# Revit family: 08101000
name_source: partatom
category: Specialty Equipment
units: mm (PartAtom-declared; Revit-internal decimal feet)

## family parameters
Always vertical = Yes
Cut with Voids When Loaded = No
Enable Cutting in Views = Yes
Maintain Annotation Orientation = No
OmniClass Number = 23.40.40.00
OmniClass Title = Food Service Equipment and Furnishings
Part Type = Normal
Room Calculation Point = No
Round Connector Dimension = Use Diameter
Shared = No
Work Plane-Based = No

## types (1)
- Standard
    Connector_1_Diameter = 24 mm  [stored 0.0787402 ft]
    Default Elevation = 0 mm  [stored 0 ft]
    Description = Kjølt brønn KBK-160-1GN
    Height = 537 mm
    Length = 427 mm
    Manufacturer = Rustfriebergh AS
    Mass = 47,00 kg
    Model = 08101000
    URL = https://www.rustfriebergh.no
    Width = 630 mm

note: [stored X ft] marks values corroborated as IEEE doubles in the binary element streams (Revit-internal decimal feet)

## geometry (parser evidence)
native form markers: Sweep x2
no freeform markers — native parametric forms only
